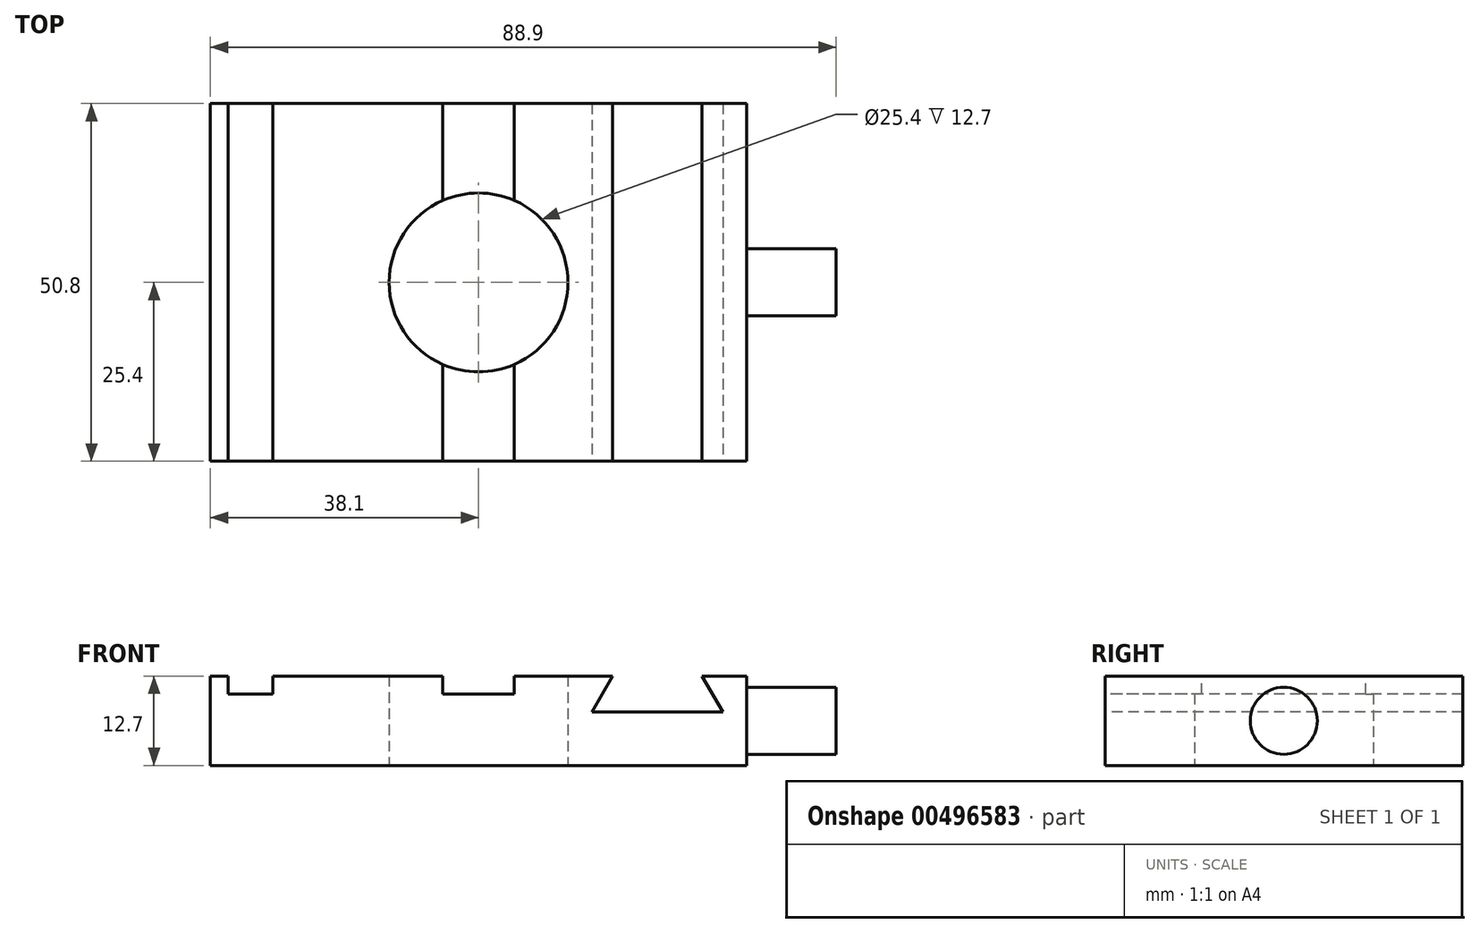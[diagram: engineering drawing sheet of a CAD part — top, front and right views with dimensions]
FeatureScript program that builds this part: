
annotation { "Feature Type Name" : "Feature", "Feature Type Description" : "" }
export const myFeature = defineFeature(function(context is Context, id is Id, definition is map)
    precondition{}
    {
        {
            var Q0;
            Q0=qCreatedBy(makeId("Top.planeOp"),FACE);
            var sketch = newSketch(context, id + "F0", { "sketchPlane" : qUnion([Q0])});
            skLineSegment(sketch, "E0.bottom", {"start": v(38.1, 25.4) * mm, "end": v(-38.1, 25.4) * mm});
            skLineSegment(sketch, "E0.top", {"start": v(38.1, -25.4) * mm, "end": v(-38.1, -25.4) * mm});
            skLineSegment(sketch, "E0.left", {"start": v(38.1, 25.4) * mm, "end": v(38.1, -25.4) * mm});
            skLineSegment(sketch, "E0.right", {"start": v(-38.1, 25.4) * mm, "end": v(-38.1, -25.4) * mm});
            skCircle(sketch, "E1", {"center": v(0, 0) * mm, "radius": 12.7 * mm});
            skSolve(sketch);
        }
        {
            var Q0;
            Q0 = qSketchRegion(id + "F0", true);
            extrude(context, id + "F1", {"entities" : qUnion([Q0]), "depth" : 12.7 * mm, "offsetDistance" : 25.4 * mm});
        }
        {
            var Q0;
            Q0=makeQuery(id+"F1.opExtrude","CAP_FACE",FACE,{"disambiguationData":[OSD([sQuery(id+"F0.wireOp",EDGE,"E0.bottom"),sQuery(id+"F0.wireOp",EDGE,"E0.top"),sQuery(id+"F0.wireOp",EDGE,"E0.left"),sQuery(id+"F0.wireOp",EDGE,"E0.right"),sQuery(id+"F0.wireOp",EDGE,"E1")])],"isStart":false});
            var sketch = newSketch(context, id + "F2", { "sketchPlane" : qUnion([Q0])});
            skLineSegment(sketch, "E2.bottom", {"start": v(-35.56, 25.4) * mm, "end": v(-29.21, 25.4) * mm});
            skLineSegment(sketch, "E2.top", {"start": v(-35.56, -25.4) * mm, "end": v(-29.21, -25.4) * mm});
            skLineSegment(sketch, "E2.left", {"start": v(-35.56, 25.4) * mm, "end": v(-35.56, -25.4) * mm});
            skLineSegment(sketch, "E2.right", {"start": v(-29.21, 25.4) * mm, "end": v(-29.21, -25.4) * mm});
            skLineSegment(sketch, "E3.bottom", {"start": v(-5.08, 25.4) * mm, "end": v(5.08, 25.4) * mm});
            skLineSegment(sketch, "E3.top", {"start": v(-5.08, -25.4) * mm, "end": v(5.08, -25.4) * mm});
            skLineSegment(sketch, "E3.left", {"start": v(-5.08, 25.4) * mm, "end": v(-5.08, -25.4) * mm});
            skLineSegment(sketch, "E3.right", {"start": v(5.08, 25.4) * mm, "end": v(5.08, -25.4) * mm});
            skPoint(sketch, "E4", {"position": v(0, 0) * mm});
            skLineSegment(sketch, "E5", {"start": v(0, 25.4) * mm, "end": v(0, -25.4) * mm, "construction": true});
            skSolve(sketch);
        }
        {
            var Q0;
            {var subQ0=sQuery(id+"F2.wireOp",EDGE,"E3.bottom");Q0=makeQuery(id+"F2.imprint","IMPRINT",FACE,{"disambiguationData":[TD([[makeQuery(id+"F2.imprint","IMPRINT",EDGE,{"derivedFrom":subQ0}),1.0]])]});}
            var Q1;
            {var subQ0=sQuery(id+"F2.wireOp",EDGE,"E3.top");Q1=makeQuery(id+"F2.imprint","IMPRINT",FACE,{"disambiguationData":[TD([[makeQuery(id+"F2.imprint","IMPRINT",EDGE,{"derivedFrom":subQ0}),-1.0]])]});}
            var Q2;
            Q2=makeQuery(id+"F2.imprint","IMPRINT",FACE,{"disambiguationData":[TD([[makeQuery(id+"F2.imprint","IMPRINT",EDGE,{"derivedFrom":sQuery(id+"F2.wireOp",EDGE,"E2.bottom")}),1.0]])]});
            extrude(context, id + "F3", {"entities" : qUnion([Q0, Q1, Q2]), "operationType" : NewBodyOperationType.REMOVE, "oppositeDirection" : true, "depth" : 2.54 * mm, "offsetDistance" : 25.4 * mm});
        }
        {
            var Q0;
            Q0=makeQuery(id+"F1.opExtrude","SWEPT_FACE",FACE,{"disambiguationData":[OSD([sQuery(id+"F0.wireOp",EDGE,"E0.top")])]});
            var sketch = newSketch(context, id + "F4", { "sketchPlane" : qUnion([Q0])});
            skLineSegment(sketch, "E6", {"start": v(19.05, 12.7) * mm, "end": v(16.12, 7.62) * mm});
            skLineSegment(sketch, "E7", {"start": v(16.12, 7.62) * mm, "end": v(34.68, 7.62) * mm});
            skLineSegment(sketch, "E8", {"start": v(34.68, 7.62) * mm, "end": v(31.75, 12.7) * mm});
            skLineSegment(sketch, "E9", {"start": v(31.75, 12.7) * mm, "end": v(19.05, 12.7) * mm});
            skLineSegment(sketch, "E10", {"start": v(25.4, 7.62) * mm, "end": v(25.4, 12.7) * mm, "construction": true});
            skSolve(sketch);
        }
        {
            var Q0;
            Q0=makeQuery(id+"F4.imprint","IMPRINT",FACE,{"disambiguationData":[TD([[makeQuery(id+"F4.imprint","IMPRINT",EDGE,{"derivedFrom":sQuery(id+"F4.wireOp",EDGE,"E6")}),1.0]])]});
            extrude(context, id + "F5", {"entities" : qUnion([Q0]), "operationType" : NewBodyOperationType.REMOVE, "endBound" : BoundingType.UP_TO_NEXT, "oppositeDirection" : true, "depth" : 25.4 * mm, "offsetDistance" : 25.4 * mm});
        }
        {
            var Q0;
            Q0=makeQuery(id+"F1.opExtrude","SWEPT_FACE",FACE,{"disambiguationData":[OSD([sQuery(id+"F0.wireOp",EDGE,"E0.left")])]});
            var sketch = newSketch(context, id + "F6", { "sketchPlane" : qUnion([Q0])});
            skCircle(sketch, "E11", {"center": v(0, 6.35) * mm, "radius": 4.76 * mm});
            skPoint(sketch, "E11.centerSnap0", {"position": v(-25.4, 6.35) * mm});
            skSolve(sketch);
        }
        {
            var Q0;
            Q0 = qSketchRegion(id + "F6", true);
            extrude(context, id + "F7", {"entities" : qUnion([Q0]), "operationType" : NewBodyOperationType.ADD, "depth" : 12.7 * mm, "offsetDistance" : 25.4 * mm});
        }
    });
